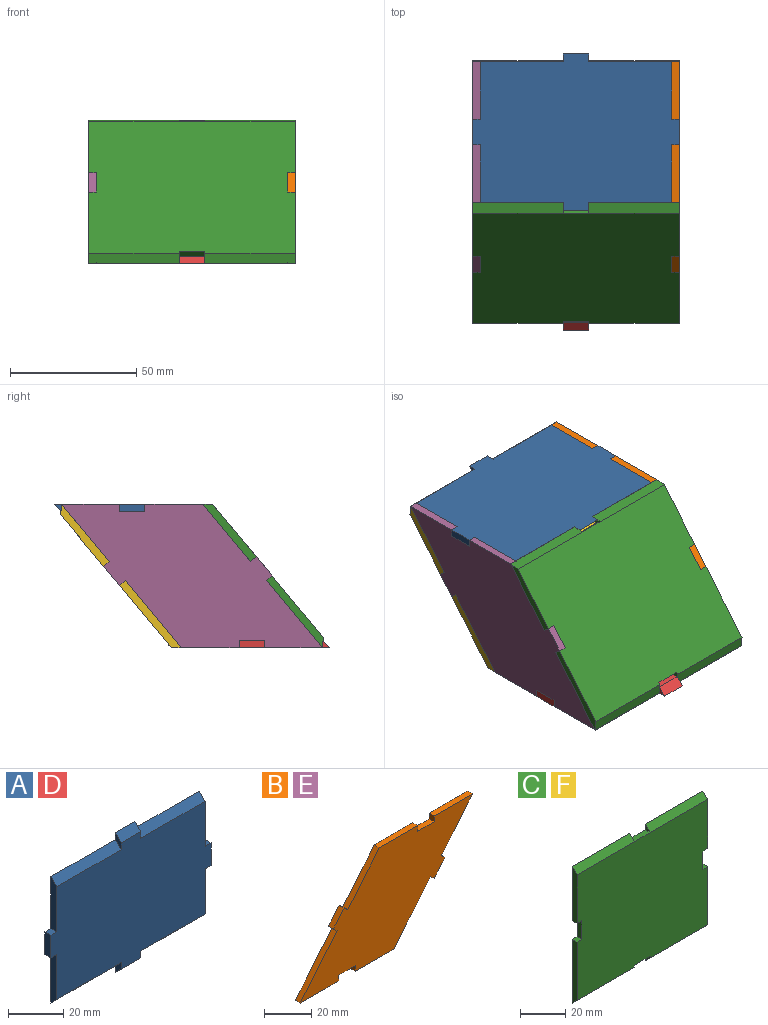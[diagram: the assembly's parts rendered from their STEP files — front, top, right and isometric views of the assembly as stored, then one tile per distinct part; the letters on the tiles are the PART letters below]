
ASSEMBLY  parts=6 mates=5
PART A: 22 faces, bbox 82x3x62 mm
  f0: plane 23x3mm, normal (1,0,0), area 64.5mm2, adj f1,f14,f15,f21
  f1: plane 3x3mm, normal (0,0,-1), area 9mm2, adj f0,f2,f14,f15
  f2: plane 10x3mm, normal (1,0,0), area 30mm2, adj f1,f3,f14,f15
  f3: plane 3x3mm, normal (0,0,1), area 9mm2, adj f2,f4,f14,f15
  f4: plane 23x3mm, normal (1,0,0), area 64.5mm2, adj f3,f14,f15,f18
  f5: plane 6x3mm, normal (1,0,0), area 9mm2, adj f14,f15,f16,f18
  f6: plane 6x3mm, normal (-1,0,0), area 9mm2, adj f14,f15,f16,f17
  f7: plane 23x3mm, normal (-1,0,0), area 64.5mm2, adj f8,f14,f15,f17
  f8: plane 3x3mm, normal (0,0,1), area 9mm2, adj f7,f9,f14,f15
  f9: plane 10x3mm, normal (-1,0,0), area 30mm2, adj f8,f10,f14,f15
  f10: plane 3x3mm, normal (0,0,-1), area 9mm2, adj f9,f11,f14,f15
  f11: plane 23x3mm, normal (-1,0,0), area 64.5mm2, adj f10,f14,f15,f20
  f12: plane 6x3mm, normal (-1,0,0), area 9mm2, adj f14,f15,f19,f20
  f13: plane 6x3mm, normal (1,0,0), area 9mm2, adj f14,f15,f19,f21
  f14: plane 82x56mm, normal (0,-1,0), area 3920mm2, adj f0,f1,f2,f3,f4,f5,f6,f7
  f15: plane 82x62mm, normal (0,1,0), area 4376mm2, adj f0,f1,f2,f3,f4,f5,f6,f7
  f16: plane 10x3mm, normal (0,-0.71,0.71), area 42.4mm2, adj f5,f6,f14,f15
  f17: plane 33x3mm, normal (0,-0.71,0.71), area 140mm2, adj f6,f7,f14,f15
  f18: plane 33x3mm, normal (0,-0.71,0.71), area 140mm2, adj f4,f5,f14,f15
  f19: plane 10x3mm, normal (0,-0.71,-0.71), area 42.4mm2, adj f12,f13,f14,f15
  f20: plane 33x3mm, normal (0,-0.71,-0.71), area 140mm2, adj f11,f12,f14,f15
  f21: plane 33x3mm, normal (0,-0.71,-0.71), area 140mm2, adj f0,f13,f14,f15
PART B: 22 faces, bbox 103.4x3x57 mm
  f0: plane 3x2.31mm, normal (-0.64,0,-0.77), area 9mm2, adj f1,f19,f20,f21
  f1: plane 26.6x22.11mm, normal (-0.77,0,0.64), area 103.8mm2, adj f0,f2,f20,f21
  f2: plane 23x3mm, normal (0,0,-1), area 69mm2, adj f1,f3,f20,f21
  f3: plane 3x3mm, normal (1,0,0), area 9mm2, adj f2,f4,f20,f21
  f4: plane 10x3mm, normal (0,0,-1), area 30mm2, adj f3,f5,f20,f21
  f5: plane 3x3mm, normal (-1,0,0), area 9mm2, adj f4,f6,f20,f21
  f6: plane 23x3mm, normal (0,0,-1), area 69mm2, adj f5,f7,f20,f21
  f7: plane 26.6x22.11mm, normal (0.77,0,-0.64), area 103.8mm2, adj f6,f8,f20,f21
  f8: plane 3x2.31mm, normal (-0.64,0,-0.77), area 9mm2, adj f7,f9,f20,f21
  f9: plane 7.69x6.39mm, normal (0.77,0,-0.64), area 30mm2, adj f8,f10,f20,f21
  f10: plane 3x2.31mm, normal (0.64,0,0.77), area 9mm2, adj f9,f11,f20,f21
  f11: plane 22.75x18.91mm, normal (0.77,0,-0.64), area 88.7mm2, adj f10,f12,f20,f21
  f12: plane 23x3mm, normal (0,0,1), area 69mm2, adj f11,f13,f20,f21
  f13: plane 3x3mm, normal (-1,0,0), area 9mm2, adj f12,f14,f20,f21
  f14: plane 10x3mm, normal (0,0,1), area 30mm2, adj f13,f15,f20,f21
  f15: plane 3x3mm, normal (1,0,0), area 9mm2, adj f14,f16,f20,f21
  f16: plane 23x3mm, normal (0,0,1), area 69mm2, adj f15,f17,f20,f21
  f17: plane 22.75x18.91mm, normal (-0.77,0,0.64), area 88.7mm2, adj f16,f18,f20,f21
  f18: plane 3x2.31mm, normal (0.64,0,0.77), area 9mm2, adj f17,f19,f20,f21
  f19: plane 7.69x6.39mm, normal (-0.77,0,0.64), area 30mm2, adj f0,f18,f20,f21
  f20: plane 103.41x57.04mm, normal (0,-1,0), area 3194mm2, adj f0,f1,f2,f3,f4,f5,f6,f7
  f21: plane 103.41x57.04mm, normal (0,1,0), area 3194mm2, adj f0,f1,f2,f3,f4,f5,f6,f7
PART C: 22 faces, bbox 82x3x74.2 mm
  f0: plane 82x68.18mm, normal (0,-1,0), area 5520.8mm2, adj f1,f2,f4,f5,f8,f9,f10,f11
  f1: plane 34.59x3mm, normal (1,0,0), area 99.3mm2, adj f0,f3,f16,f20
  f2: plane 34.59x3mm, normal (-1,0,0), area 99.3mm2, adj f0,f3,f15,f21
  f3: plane 82x74.18mm, normal (0,1,0), area 5952.8mm2, adj f1,f2,f4,f5,f6,f7,f8,f9
  f4: plane 10x3mm, normal (1,0,0), area 30mm2, adj f0,f3,f14,f16
  f5: plane 10x3mm, normal (-1,0,0), area 30mm2, adj f0,f3,f13,f15
  f6: plane 3x3mm, normal (1,0,0), area 4.5mm2, adj f3,f9,f12
  f7: plane 3x3mm, normal (-1,0,0), area 4.5mm2, adj f3,f8,f12
  f8: plane 36x3mm, normal (0,-0.71,0.71), area 152.7mm2, adj f0,f3,f7,f10
  f9: plane 36x3mm, normal (0,-0.71,0.71), area 152.7mm2, adj f0,f3,f6,f11
  f10: plane 29.59x3mm, normal (1,0,0), area 84.3mm2, adj f0,f3,f8,f14
  f11: plane 29.59x3mm, normal (-1,0,0), area 84.3mm2, adj f0,f3,f9,f13
  f12: plane 10x3mm, normal (0,0,1), area 30mm2, adj f0,f3,f6,f7
  f13: plane 3x3mm, normal (0,0,-1), area 9mm2, adj f0,f3,f5,f11
  f14: plane 3x3mm, normal (0,0,-1), area 9mm2, adj f0,f3,f4,f10
  f15: plane 3x3mm, normal (0,0,1), area 9mm2, adj f0,f2,f3,f5
  f16: plane 3x3mm, normal (0,0,1), area 9mm2, adj f0,f1,f3,f4
  f17: plane 4x3mm, normal (1,0,0), area 7.5mm2, adj f0,f3,f19,f21
  f18: plane 4x3mm, normal (-1,0,0), area 7.5mm2, adj f0,f3,f19,f20
  f19: plane 10x3mm, normal (0,0,-1), area 30mm2, adj f0,f3,f17,f18
  f20: plane 36x3mm, normal (0,-0.71,-0.71), area 152.7mm2, adj f0,f1,f3,f18
  f21: plane 36x3mm, normal (0,-0.71,-0.71), area 152.7mm2, adj f0,f2,f3,f17
PART D: same geometry as A
PART E: same geometry as B
PART F: same geometry as C
PLACE A rot(axis=(1,0,0),90deg) t=(-15.35,39.99,57.69)mm
PLACE B rot(axis=(0,0,1),90deg) t=(22.65,-7.56,0.65)mm
PLACE C rot(axis=(-1,0,0),39.7deg) t=(-15.35,-15.24,24.94)mm
PLACE D rot(axis=(-1,0,0),90deg) t=(-15.35,-7.42,0.65)mm fixed
PLACE E rot(axis=(0,0,1),90deg) t=(-56.35,-7.56,0.65)mm
PLACE F rot(axis=(0,-0.34,-0.94),180deg) t=(-15.35,40.76,24.94)mm
MATE fastened D.f8 <-> E.f5  axis (0,1,0) through (-56.35,-2.42,2.15)mm
MATE fastened F.f3 <-> E.f11  axis (0,-0.77,0.64) through (-56.35,58.53,46.32)mm
MATE fastened C.f3 <-> B.f17  axis (0,0.77,-0.64) through (25.65,2.53,46.32)mm
MATE fastened D.f1 <-> B.f3  axis (0,-1,0) through (25.65,-12.42,2.15)mm
MATE fastened A.f8 <-> E.f15  axis (0,-1,0) through (-56.35,34.99,56.19)mm
